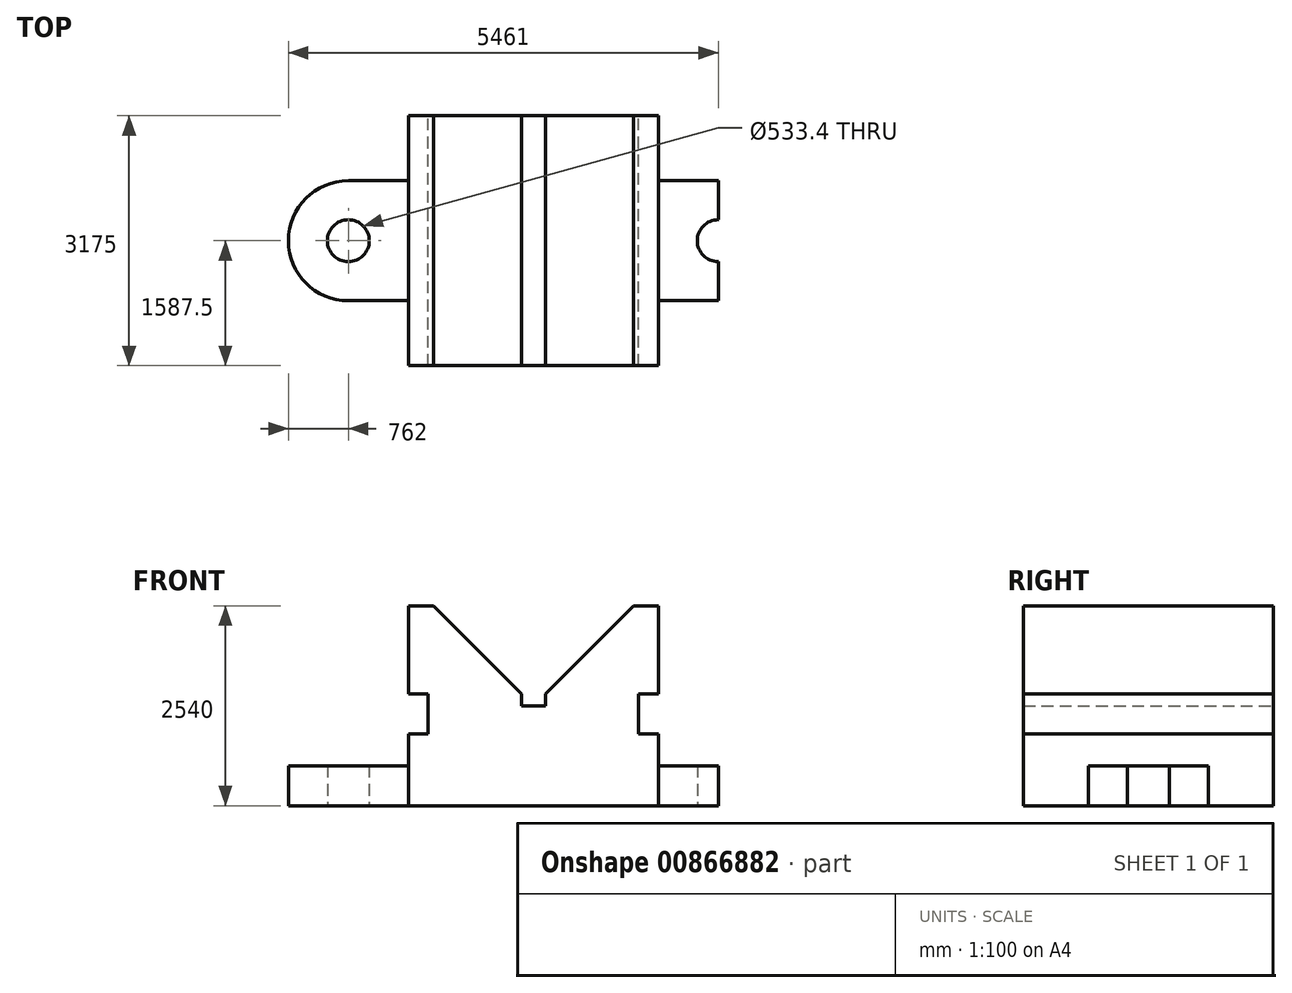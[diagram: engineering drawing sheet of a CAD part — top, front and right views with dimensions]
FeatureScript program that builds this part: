
annotation { "Feature Type Name" : "Feature", "Feature Type Description" : "" }
export const myFeature = defineFeature(function(context is Context, id is Id, definition is map)
    precondition{}
    {
        {
            var Q0;
            Q0=qCreatedBy(makeId("Front.planeOp"),FACE);
            var sketch = newSketch(context, id + "F0", { "sketchPlane" : qUnion([Q0])});
            skLineSegment(sketch, "E0.bottom", {"start": v(0, 0) * mm, "end": v(3175, 0) * mm});
            skLineSegment(sketch, "E0.top", {"start": v(0, 2540) * mm, "end": v(3175, 2540) * mm});
            skLineSegment(sketch, "E0.left", {"start": v(0, 0) * mm, "end": v(0, 2540) * mm});
            skLineSegment(sketch, "E0.right", {"start": v(3175, 0) * mm, "end": v(3175, 2540) * mm});
            skLineSegment(sketch, "E1", {"start": v(0, 2540) * mm, "end": v(317.5, 2540) * mm});
            skLineSegment(sketch, "E2", {"start": v(3175, 2540) * mm, "end": v(2857.5, 2540) * mm});
            skLineSegment(sketch, "E3", {"start": v(2857.5, 2540) * mm, "end": v(1739.9, 1422.4) * mm});
            skLineSegment(sketch, "E4", {"start": v(1435.1, 1422.4) * mm, "end": v(317.5, 2540) * mm});
            skLineSegment(sketch, "E5", {"start": v(1587.5, 1270) * mm, "end": v(1739.9, 1270) * mm});
            skLineSegment(sketch, "E6", {"start": v(1587.5, 1270) * mm, "end": v(1435.1, 1270) * mm});
            skLineSegment(sketch, "E7.bottom", {"start": v(1435.1, 1270) * mm, "end": v(1739.9, 1270) * mm});
            skLineSegment(sketch, "E7.top", {"start": v(1435.1, 1422.4) * mm, "end": v(1739.9, 1422.4) * mm});
            skLineSegment(sketch, "E7.left", {"start": v(1435.1, 1270) * mm, "end": v(1435.1, 1422.4) * mm});
            skLineSegment(sketch, "E7.right", {"start": v(1739.9, 1270) * mm, "end": v(1739.9, 1422.4) * mm});
            skLineSegment(sketch, "E8", {"start": v(0, 2540) * mm, "end": v(0, 1422.4) * mm});
            skLineSegment(sketch, "E9.bottom", {"start": v(0, 1422.4) * mm, "end": v(254, 1422.4) * mm});
            skLineSegment(sketch, "E9.top", {"start": v(0, 914.4) * mm, "end": v(254, 914.4) * mm});
            skLineSegment(sketch, "E9.left", {"start": v(0, 1422.4) * mm, "end": v(0, 914.4) * mm});
            skLineSegment(sketch, "E9.right", {"start": v(254, 1422.4) * mm, "end": v(254, 914.4) * mm});
            skLineSegment(sketch, "E10", {"start": v(3175, 2540) * mm, "end": v(3175, 1422.4) * mm});
            skLineSegment(sketch, "E11.bottom", {"start": v(3175, 1422.4) * mm, "end": v(2921, 1422.4) * mm});
            skLineSegment(sketch, "E11.top", {"start": v(3175, 914.4) * mm, "end": v(2921, 914.4) * mm});
            skLineSegment(sketch, "E11.left", {"start": v(3175, 1422.4) * mm, "end": v(3175, 914.4) * mm});
            skLineSegment(sketch, "E11.right", {"start": v(2921, 1422.4) * mm, "end": v(2921, 914.4) * mm});
            skSolve(sketch);
        }
        {
            var Q0;
            Q0=makeQuery(id+"F0.imprint","IMPRINT",FACE,{"disambiguationData":[TD([[makeQuery(id+"F0.imprint","IMPRINT",EDGE,{"derivedFrom":sQuery(id+"F0.wireOp",EDGE,"E0.bottom")}),1.0]])]});
            extrude(context, id + "F1", {"entities" : qUnion([Q0]), "endBound" : BoundingType.SYMMETRIC, "depth" : 3175 * mm, "offsetDistance" : 25.4 * mm});
        }
        {
            var Q0;
            Q0=makeQuery(id+"F1.opExtrude","SWEPT_FACE",FACE,{"disambiguationData":[OSD([sQuery(id+"F0.wireOp",EDGE,"E0.bottom")])]});
            var sketch = newSketch(context, id + "F2", { "sketchPlane" : qUnion([Q0])});
            skLineSegment(sketch, "E12", {"start": v(0, 0) * mm, "end": v(0, 762) * mm});
            skLineSegment(sketch, "E13.bottom", {"start": v(0, 762) * mm, "end": v(-762, 762) * mm});
            skLineSegment(sketch, "E13.top", {"start": v(0, -762) * mm, "end": v(-762, -762) * mm});
            skLineSegment(sketch, "E13.left", {"start": v(0, 762) * mm, "end": v(0, -762) * mm});
            skLineSegment(sketch, "E13.right", {"start": v(-762, 762) * mm, "end": v(-762, -762) * mm});
            skArc(sketch, "E14", {"start": v(-762, 762) * mm, "mid": v(-1524, 0) * mm, "end": v(-762, -762) * mm});
            skCircle(sketch, "E15", {"center": v(-762, 0) * mm, "radius": 266.7 * mm});
            skLineSegment(sketch, "E16.bottom", {"start": v(3175, 762) * mm, "end": v(3937, 762) * mm});
            skLineSegment(sketch, "E16.top", {"start": v(3175, -762) * mm, "end": v(3937, -762) * mm});
            skLineSegment(sketch, "E16.left", {"start": v(3175, 762) * mm, "end": v(3175, -762) * mm});
            skLineSegment(sketch, "E16.right", {"start": v(3937, 762) * mm, "end": v(3937, -762) * mm});
            skArc(sketch, "E17", {"start": v(3937, 762) * mm, "mid": v(4699, 0) * mm, "end": v(3937, -762) * mm});
            skCircle(sketch, "E18", {"center": v(3937, 0) * mm, "radius": 266.7 * mm});
            skSolve(sketch);
        }
        {
            var Q0;
            {var subQ0=sQuery(id+"F2.wireOp",EDGE,"E14");Q0=makeQuery(id+"F2.imprint","IMPRINT",FACE,{"disambiguationData":[TD([[makeQuery(id+"F2.imprint","IMPRINT",EDGE,{"derivedFrom":subQ0}),1.0]])]});}
            var Q1;
            {var subQ4=sQuery(id+"F2.wireOp",EDGE,"E13.bottom");Q1=makeQuery(id+"F2.imprint","IMPRINT",FACE,{"disambiguationData":[TD([[makeQuery(id+"F2.imprint","IMPRINT",EDGE,{"derivedFrom":subQ4}),1.0]])]});}
            var Q2;
            {var subQ2=sQuery(id+"F2.wireOp",EDGE,"E16.bottom");Q2=makeQuery(id+"F2.imprint","IMPRINT",FACE,{"disambiguationData":[TD([[makeQuery(id+"F2.imprint","IMPRINT",EDGE,{"derivedFrom":subQ2}),-1.0]])]});}
            var Q3;
            {var subQ0=sQuery(id+"F2.wireOp",EDGE,"E17");Q3=makeQuery(id+"F2.imprint","IMPRINT",FACE,{"disambiguationData":[TD([[makeQuery(id+"F2.imprint","IMPRINT",EDGE,{"derivedFrom":subQ0}),-1.0]])]});}
            extrude(context, id + "F3", {"entities" : qUnion([Q0, Q1, Q2, Q3]), "operationType" : NewBodyOperationType.ADD, "oppositeDirection" : true, "depth" : 508 * mm, "offsetDistance" : 25.4 * mm});
        }
    });
